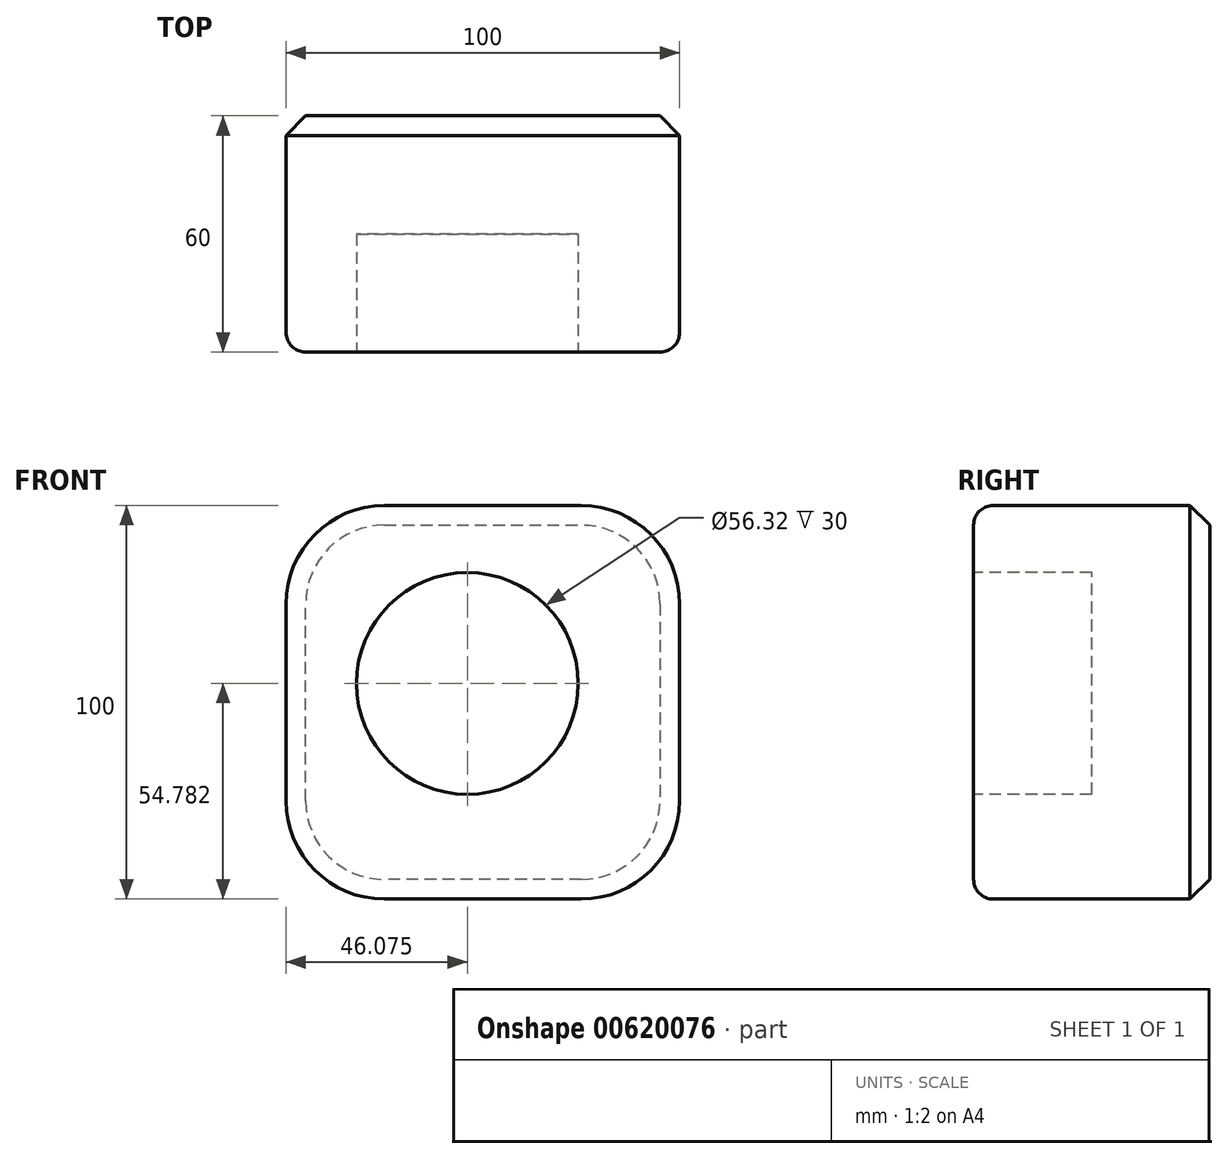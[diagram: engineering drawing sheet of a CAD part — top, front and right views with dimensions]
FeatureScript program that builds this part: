
annotation { "Feature Type Name" : "Feature", "Feature Type Description" : "" }
export const myFeature = defineFeature(function(context is Context, id is Id, definition is map)
    precondition{}
    {
        {
            var Q0;
            Q0=qCreatedBy(makeId("Front.planeOp"),FACE);
            var sketch = newSketch(context, id + "F0", { "sketchPlane" : qUnion([Q0])});
            skLineSegment(sketch, "E0.bottom", {"start": v(-0.18, 83.25) * mm, "end": v(49.82, 83.25) * mm});
            skLineSegment(sketch, "E0.top", {"start": v(-0.18, -16.75) * mm, "end": v(49.82, -16.75) * mm});
            skLineSegment(sketch, "E0.left", {"start": v(-25.18, 58.25) * mm, "end": v(-25.18, 8.25) * mm});
            skLineSegment(sketch, "E0.right", {"start": v(74.82, 58.25) * mm, "end": v(74.82, 8.25) * mm});
            skPoint(sketch, "E1.visualSharp", {"position": v(-25.18, 83.25) * mm});
            skArc(sketch, "E1.filletArc", {"start": v(-0.18, 83.25) * mm, "mid": v(-17.86, 75.93) * mm, "end": v(-25.18, 58.25) * mm});
            skPoint(sketch, "E2.visualSharp", {"position": v(74.82, 83.25) * mm});
            skArc(sketch, "E2.filletArc", {"start": v(74.82, 58.25) * mm, "mid": v(67.5, 75.93) * mm, "end": v(49.82, 83.25) * mm});
            skPoint(sketch, "E3.visualSharp", {"position": v(74.82, -16.75) * mm});
            skArc(sketch, "E3.filletArc", {"start": v(49.82, -16.75) * mm, "mid": v(67.5, -9.43) * mm, "end": v(74.82, 8.25) * mm});
            skPoint(sketch, "E4.visualSharp", {"position": v(-25.18, -16.75) * mm});
            skArc(sketch, "E4.filletArc", {"start": v(-25.18, 8.25) * mm, "mid": v(-17.86, -9.43) * mm, "end": v(-0.18, -16.75) * mm});
            skSolve(sketch);
        }
        {
            var Q0;
            Q0 = qSketchRegion(id + "F0", true);
            extrude(context, id + "F1", {"entities" : qUnion([Q0]), "depth" : 60 * mm, "offsetDistance" : 25 * mm});
        }
        {
            var Q0;
            Q0=makeQuery(id+"F1.opExtrude","CAP_FACE",FACE,{"disambiguationData":[OSD([sQuery(id+"F0.wireOp",EDGE,"E0.bottom"),sQuery(id+"F0.wireOp",EDGE,"E0.top"),sQuery(id+"F0.wireOp",EDGE,"E0.left"),sQuery(id+"F0.wireOp",EDGE,"E0.right"),sQuery(id+"F0.wireOp",EDGE,"E1.filletArc"),sQuery(id+"F0.wireOp",EDGE,"E2.filletArc"),sQuery(id+"F0.wireOp",EDGE,"E3.filletArc"),sQuery(id+"F0.wireOp",EDGE,"E4.filletArc")])],"isStart":false});
            fillet(context, id + "F2", {"entities" : qUnion([Q0]), "radius" : 5 * mm, "tangentPropagation" : true, "allowEdgeOverflow" : false});
        }
        {
            var Q0;
            Q0=makeQuery(id+"F1.opExtrude","CAP_FACE",FACE,{"disambiguationData":[OSD([sQuery(id+"F0.wireOp",EDGE,"E0.bottom"),sQuery(id+"F0.wireOp",EDGE,"E0.top"),sQuery(id+"F0.wireOp",EDGE,"E0.left"),sQuery(id+"F0.wireOp",EDGE,"E0.right"),sQuery(id+"F0.wireOp",EDGE,"E1.filletArc"),sQuery(id+"F0.wireOp",EDGE,"E2.filletArc"),sQuery(id+"F0.wireOp",EDGE,"E3.filletArc"),sQuery(id+"F0.wireOp",EDGE,"E4.filletArc")])],"isStart":true});
            chamfer(context, id + "F3", {"entities" : qUnion([Q0]), "width" : 5 * mm, "tangentPropagation" : true});
        }
        {
            var Q0;
            Q0=makeQuery(id+"F1.opExtrude","CAP_FACE",FACE,{"disambiguationData":[OSD([sQuery(id+"F0.wireOp",EDGE,"E0.bottom"),sQuery(id+"F0.wireOp",EDGE,"E0.top"),sQuery(id+"F0.wireOp",EDGE,"E0.left"),sQuery(id+"F0.wireOp",EDGE,"E0.right"),sQuery(id+"F0.wireOp",EDGE,"E1.filletArc"),sQuery(id+"F0.wireOp",EDGE,"E2.filletArc"),sQuery(id+"F0.wireOp",EDGE,"E3.filletArc"),sQuery(id+"F0.wireOp",EDGE,"E4.filletArc")])],"isStart":false});
            var sketch = newSketch(context, id + "F4", { "sketchPlane" : qUnion([Q0])});
            skCircle(sketch, "E5", {"center": v(20.9, 38.03) * mm, "radius": 28.16 * mm});
            skSolve(sketch);
        }
        {
            var Q0;
            Q0 = qSketchRegion(id + "F4", true);
            extrude(context, id + "F5", {"entities" : qUnion([Q0]), "operationType" : NewBodyOperationType.REMOVE, "oppositeDirection" : true, "depth" : 30 * mm, "offsetDistance" : 25 * mm});
        }
    });
